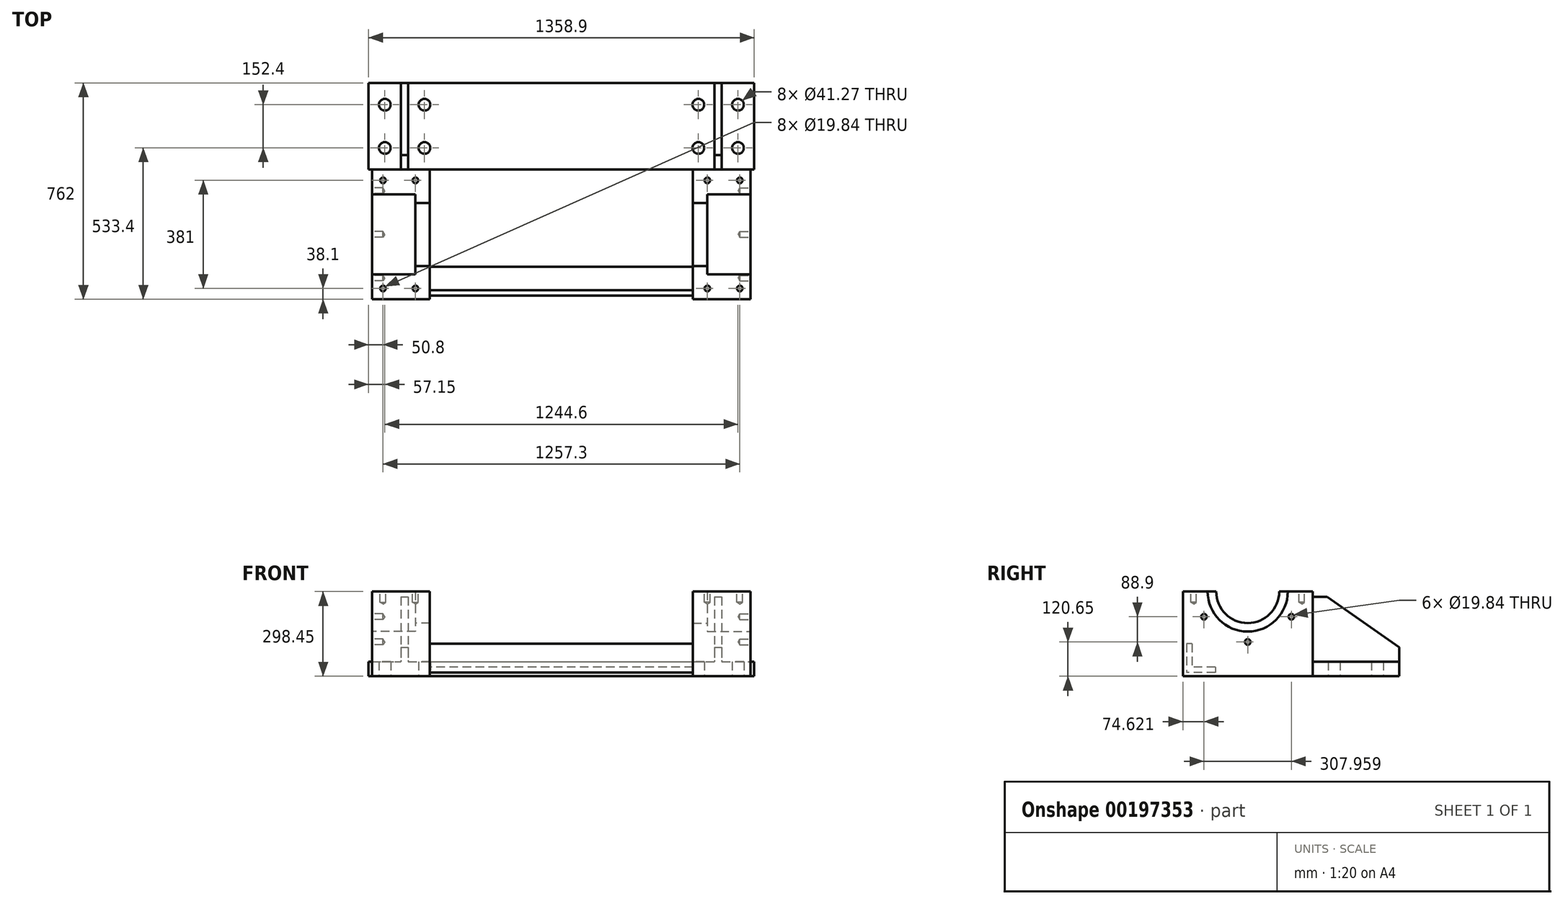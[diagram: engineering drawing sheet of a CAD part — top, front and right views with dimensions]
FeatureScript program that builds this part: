
annotation { "Feature Type Name" : "Feature", "Feature Type Description" : "" }
export const myFeature = defineFeature(function(context is Context, id is Id, definition is map)
    precondition{}
    {
        {
            var Q0;
            Q0=qCreatedBy(makeId("Top.planeOp"),FACE);
            var sketch = newSketch(context, id + "F0", { "sketchPlane" : qUnion([Q0])});
            skLineSegment(sketch, "E0.bottom", {"start": v(-679.45, 152.4) * mm, "end": v(679.45, 152.4) * mm});
            skLineSegment(sketch, "E0.top", {"start": v(-679.45, -152.4) * mm, "end": v(679.45, -152.4) * mm});
            skLineSegment(sketch, "E0.left", {"start": v(-679.45, 152.4) * mm, "end": v(-679.45, -152.4) * mm});
            skLineSegment(sketch, "E0.right", {"start": v(679.45, 152.4) * mm, "end": v(679.45, -152.4) * mm});
            skPoint(sketch, "E0.middle", {"position": v(0, 0) * mm});
            skLineSegment(sketch, "E1", {"start": v(0, 355.28) * mm, "end": v(0, -340.56) * mm, "construction": true});
            skLineSegment(sketch, "E2.0", {"start": v(-482.6, 355.28) * mm, "end": v(-482.6, -340.56) * mm, "construction": true});
            skLineSegment(sketch, "E3.0", {"start": v(-622.3, 355.28) * mm, "end": v(-622.3, -340.56) * mm, "construction": true});
            skLineSegment(sketch, "E4.0", {"start": v(-679.45, -76.2) * mm, "end": v(679.45, -76.2) * mm, "construction": true});
            skLineSegment(sketch, "E5.0", {"start": v(-679.45, 76.2) * mm, "end": v(679.45, 76.2) * mm, "construction": true});
            skCircle(sketch, "E6", {"center": v(-622.3, 76.2) * mm, "radius": 20.64 * mm});
            skCircle(sketch, "E7.0.1.0", {"center": v(-622.3, -76.2) * mm, "radius": 20.64 * mm});
            skCircle(sketch, "E7.1.0.0", {"center": v(-482.6, 76.2) * mm, "radius": 20.64 * mm});
            skCircle(sketch, "E7.1.1.0", {"center": v(-482.6, -76.2) * mm, "radius": 20.64 * mm});
            skLineSegment(sketch, "E7.direction1", {"start": v(-622.3, 76.2) * mm, "end": v(-482.6, 76.2) * mm, "construction": true});
            skLineSegment(sketch, "E7.direction2", {"start": v(-622.3, 76.2) * mm, "end": v(-622.3, -76.2) * mm, "construction": true});
            skLineSegment(sketch, "E8.MirrorCS", {"start": v(622.3, 76.2) * mm, "end": v(622.3, -76.2) * mm, "construction": true});
            skLineSegment(sketch, "E9.MirrorCS", {"start": v(622.3, 76.2) * mm, "end": v(482.6, 76.2) * mm, "construction": true});
            skCircle(sketch, "E10.MirrorC", {"center": v(482.6, -76.2) * mm, "radius": 20.64 * mm});
            skCircle(sketch, "E11.MirrorC", {"center": v(482.6, 76.2) * mm, "radius": 20.64 * mm});
            skCircle(sketch, "E12.MirrorC", {"center": v(622.3, -76.2) * mm, "radius": 20.64 * mm});
            skCircle(sketch, "E13.MirrorC", {"center": v(622.3, 76.2) * mm, "radius": 20.64 * mm});
            skSolve(sketch);
        }
        {
            var Q0;
            Q0 = qSketchRegion(id + "F0", true);
            extrude(context, id + "F1", {"entities" : qUnion([Q0]), "depth" : 50.8 * mm});
        }
        {
            var Q0;
            Q0=makeQuery(id+"F1.opExtrude","CAP_FACE",FACE,{"disambiguationData":[OSD([sQuery(id+"F0.wireOp",EDGE,"E0.bottom"),sQuery(id+"F0.wireOp",EDGE,"E0.top"),sQuery(id+"F0.wireOp",EDGE,"E0.left"),sQuery(id+"F0.wireOp",EDGE,"E0.right"),sQuery(id+"F0.wireOp",EDGE,"E6"),sQuery(id+"F0.wireOp",EDGE,"E7.0.1.0"),sQuery(id+"F0.wireOp",EDGE,"E7.1.0.0"),sQuery(id+"F0.wireOp",EDGE,"E7.1.1.0"),sQuery(id+"F0.wireOp",EDGE,"E10.MirrorC"),sQuery(id+"F0.wireOp",EDGE,"E11.MirrorC"),sQuery(id+"F0.wireOp",EDGE,"E12.MirrorC"),sQuery(id+"F0.wireOp",EDGE,"E13.MirrorC")])],"isStart":false});
            var sketch = newSketch(context, id + "F2", { "sketchPlane" : qUnion([Q0])});
            skLineSegment(sketch, "E14", {"start": v(0, 288.05) * mm, "end": v(0, -308.88) * mm, "construction": true});
            skLineSegment(sketch, "E15.0", {"start": v(-539.75, 288.05) * mm, "end": v(-539.75, -308.88) * mm, "construction": true});
            skLineSegment(sketch, "E16.0", {"start": v(-679.45, 152.4) * mm, "end": v(679.45, 152.4) * mm, "construction": true});
            skLineSegment(sketch, "E17.0", {"start": v(-679.45, -152.4) * mm, "end": v(679.45, -152.4) * mm, "construction": true});
            skLineSegment(sketch, "E18.bottom", {"start": v(-539.75, 152.4) * mm, "end": v(-565.15, 152.4) * mm});
            skLineSegment(sketch, "E18.top", {"start": v(-539.75, -152.4) * mm, "end": v(-565.15, -152.4) * mm});
            skLineSegment(sketch, "E18.left", {"start": v(-539.75, 152.4) * mm, "end": v(-539.75, -152.4) * mm});
            skLineSegment(sketch, "E18.right", {"start": v(-565.15, 152.4) * mm, "end": v(-565.15, -152.4) * mm});
            skLineSegment(sketch, "E19.MirrorCS", {"start": v(539.75, -152.4) * mm, "end": v(565.15, -152.4) * mm});
            skLineSegment(sketch, "E20.MirrorCS", {"start": v(539.75, 152.4) * mm, "end": v(565.15, 152.4) * mm});
            skLineSegment(sketch, "E21.MirrorCS", {"start": v(565.15, 152.4) * mm, "end": v(565.15, -152.4) * mm});
            skLineSegment(sketch, "E22.MirrorCS", {"start": v(539.75, 152.4) * mm, "end": v(539.75, -152.4) * mm});
            skSolve(sketch);
        }
        {
            var Q0;
            Q0 = qSketchRegion(id + "F2", true);
            extrude(context, id + "F3", {"entities" : qUnion([Q0]), "operationType" : NewBodyOperationType.ADD, "depth" : 228.6 * mm});
        }
        {
            var Q0;
            Q0=makeQuery(id+"F3.opExtrude","SWEPT_FACE",FACE,{"disambiguationData":[OSD([sQuery(id+"F2.wireOp",EDGE,"E21.MirrorCS")])]});
            var sketch = newSketch(context, id + "F4", { "sketchPlane" : qUnion([Q0])});
            skLineSegment(sketch, "E23.0", {"start": v(152.4, 50.8) * mm, "end": v(-152.4, 50.8) * mm, "construction": true});
            skLineSegment(sketch, "E24.0", {"start": v(-152.4, 279.4) * mm, "end": v(-152.4, 50.8) * mm, "construction": true});
            skLineSegment(sketch, "E25.0", {"start": v(-101.6, 279.4) * mm, "end": v(-101.6, 50.8) * mm, "construction": true});
            skLineSegment(sketch, "E26.0", {"start": v(152.4, 101.6) * mm, "end": v(-152.4, 101.6) * mm, "construction": true});
            skLineSegment(sketch, "E27", {"start": v(-101.6, 279.4) * mm, "end": v(152.4, 101.6) * mm});
            skLineSegment(sketch, "E28", {"start": v(152.4, 279.4) * mm, "end": v(152.4, 101.6) * mm});
            skLineSegment(sketch, "E29", {"start": v(152.4, 279.4) * mm, "end": v(-101.6, 279.4) * mm});
            skSolve(sketch);
        }
        {
            var Q0;
            Q0 = qSketchRegion(id + "F4", true);
            extrude(context, id + "F5", {"entities" : qUnion([Q0]), "operationType" : NewBodyOperationType.REMOVE, "endBound" : BoundingType.THROUGH_ALL, "oppositeDirection" : true, "depth" : 25.4 * mm});
        }
        {
            var Q0;
            Q0=makeQuery(id+"F1.opExtrude","CAP_FACE",FACE,{"disambiguationData":[OSD([sQuery(id+"F0.wireOp",EDGE,"E0.bottom"),sQuery(id+"F0.wireOp",EDGE,"E0.top"),sQuery(id+"F0.wireOp",EDGE,"E0.left"),sQuery(id+"F0.wireOp",EDGE,"E0.right"),sQuery(id+"F0.wireOp",EDGE,"E6"),sQuery(id+"F0.wireOp",EDGE,"E7.0.1.0"),sQuery(id+"F0.wireOp",EDGE,"E7.1.0.0"),sQuery(id+"F0.wireOp",EDGE,"E7.1.1.0"),sQuery(id+"F0.wireOp",EDGE,"E10.MirrorC"),sQuery(id+"F0.wireOp",EDGE,"E11.MirrorC"),sQuery(id+"F0.wireOp",EDGE,"E12.MirrorC"),sQuery(id+"F0.wireOp",EDGE,"E13.MirrorC")])],"isStart":true});
            var sketch = newSketch(context, id + "F6", { "sketchPlane" : qUnion([Q0])});
            skLineSegment(sketch, "E30", {"start": v(0, -264.01) * mm, "end": v(0, 609.6) * mm, "construction": true});
            skLineSegment(sketch, "E31.0", {"start": v(-679.45, 152.4) * mm, "end": v(679.45, 152.4) * mm, "construction": true});
            skLineSegment(sketch, "E32.0", {"start": v(-679.45, 609.6) * mm, "end": v(679.45, 609.6) * mm, "construction": true});
            skLineSegment(sketch, "E33.0", {"start": v(666.75, 152.4) * mm, "end": v(666.75, 609.6) * mm});
            skLineSegment(sketch, "E34.0", {"start": v(463.55, 152.4) * mm, "end": v(463.55, 609.6) * mm});
            skLineSegment(sketch, "E35.bottom", {"start": v(463.55, 152.4) * mm, "end": v(666.75, 152.4) * mm});
            skLineSegment(sketch, "E35.top", {"start": v(463.55, 609.6) * mm, "end": v(666.75, 609.6) * mm});
            skSolve(sketch);
        }
        {
            var Q0;
            Q0 = qSketchRegion(id + "F6", true);
            extrude(context, id + "F7", {"entities" : qUnion([Q0]), "oppositeDirection" : true, "depth" : 298.45 * mm});
        }
        {
            var Q0;
            Q0=makeQuery(id+"F7.opExtrude","SWEPT_FACE",FACE,{"disambiguationData":[OSD([sQuery(id+"F6.wireOp",EDGE,"E33.0")])]});
            var sketch = newSketch(context, id + "F8", { "sketchPlane" : qUnion([Q0])});
            skCircle(sketch, "E36", {"center": v(-381, 298.45) * mm, "radius": 141.29 * mm});
            skSolve(sketch);
        }
        {
            var Q0;
            Q0 = qSketchRegion(id + "F8", true);
            extrude(context, id + "F9", {"entities" : qUnion([Q0]), "operationType" : NewBodyOperationType.REMOVE, "oppositeDirection" : true, "depth" : 152.4 * mm});
        }
        {
            var Q0;
            Q0=makeQuery(id+"F9.boolean.opBoolean","COPY",FACE,{"derivedFrom":makeQuery(id+"F9.opExtrude","CAP_FACE",FACE,{"disambiguationData":[OSD([sQuery(id+"F8.wireOp",EDGE,"E36")])],"isStart":false})});
            var sketch = newSketch(context, id + "F10", { "sketchPlane" : qUnion([Q0])});
            skCircle(sketch, "E37", {"center": v(-381, 298.45) * mm, "radius": 111.13 * mm});
            skSolve(sketch);
        }
        {
            var Q0;
            Q0 = qSketchRegion(id + "F10", true);
            extrude(context, id + "F11", {"entities" : qUnion([Q0]), "operationType" : NewBodyOperationType.REMOVE, "endBound" : BoundingType.THROUGH_ALL, "oppositeDirection" : true, "depth" : 25.4 * mm});
        }
        {
            var Q0;
            Q0=makeQuery(id+"F7.opExtrude","SWEPT_FACE",FACE,{"disambiguationData":[OSD([sQuery(id+"F6.wireOp",EDGE,"E33.0")])]});
            var sketch = newSketch(context, id + "F12", { "sketchPlane" : qUnion([Q0])});
            skLineSegment(sketch, "E38", {"start": v(-522.29, 298.45) * mm, "end": v(-239.71, 298.45) * mm, "construction": true});
            skCircle(sketch, "E39", {"center": v(-381, 298.45) * mm, "radius": 177.8 * mm, "construction": true});
            skLineSegment(sketch, "E40", {"start": v(-381, 298.45) * mm, "end": v(-381, 120.65) * mm, "construction": true});
            skPoint(sketch, "E41", {"position": v(-381, 120.65) * mm});
            skPoint(sketch, "E42.1.0", {"position": v(-227.02, 209.55) * mm});
            skPoint(sketch, "E42.2.0", {"position": v(-227.02, 387.35) * mm});
            skPoint(sketch, "E42.3.0", {"position": v(-381, 476.25) * mm});
            skPoint(sketch, "E42.4.0", {"position": v(-534.98, 387.35) * mm});
            skPoint(sketch, "E42.5.0", {"position": v(-534.98, 209.55) * mm});
            skSolve(sketch);
        }
        {
            var Q0;
            Q0=sQuery(id+"F12.wireOp",VERTEX,"E42.5.0");
            var Q1;
            Q1=sQuery(id+"F12.wireOp",VERTEX,"E41");
            var Q2;
            Q2=sQuery(id+"F12.wireOp",VERTEX,"E42.1.0");
            var Q3;
            Q3=makeQuery(id+"F7.opExtrude","SWEPT_BODY",BODY,{"disambiguationData":[OSD([sQuery(id+"F6.wireOp",EDGE,"E35.bottom"),sQuery(id+"F6.wireOp",EDGE,"E35.top"),sQuery(id+"F6.wireOp",EDGE,"E34.0"),sQuery(id+"F6.wireOp",EDGE,"E33.0")])]});
            hole(context, id + "F13", {"style" : HoleStyle.SIMPLE, "endStyle" : HoleEndStyle.BLIND, "standardTappedOrClearance" : lookupTablePath({ "standard" : "ANSI", "fit" : "Normal (ASME)", "size" : "3/4", "type" : "Clearance" }), "standardBlindInLast" : lookupTablePath({ "fit" : "Free", "standard" : "ANSI", "size" : "3/4", "type" : "Clearance" }), "holeDiameter" : 19.84 * mm, "holeDepth" : 38.1 * mm, "locations" : qUnion([Q0, Q1, Q2]), "scope" : qUnion([Q3])});
        }
        {
            var Q0;
            {var subQ1=sQuery(id+"F6.wireOp",EDGE,"E33.0");var subQ2=sQuery(id+"F6.wireOp",EDGE,"E34.0");var subQ3=sQuery(id+"F6.wireOp",EDGE,"E35.top");Q0=makeQuery(id+"F11.boolean.opBoolean","SPLIT",FACE,{"disambiguationData":[TD([makeQuery(id+"F7.opExtrude","SWEPT_FACE",FACE,{"disambiguationData":[OSD([subQ3])]})])],"derivedFrom":makeQuery(id+"F7.opExtrude","CAP_FACE",FACE,{"disambiguationData":[OSD([sQuery(id+"F6.wireOp",EDGE,"E35.bottom"),subQ3,subQ2,subQ1])],"isStart":false})});}
            var sketch = newSketch(context, id + "F14", { "sketchPlane" : qUnion([Q0])});
            skLineSegment(sketch, "E43.0", {"start": v(666.75, -152.4) * mm, "end": v(666.75, -609.6) * mm, "construction": true});
            skLineSegment(sketch, "E44.0.0", {"start": v(514.35, -522.29) * mm, "end": v(514.35, -239.71) * mm, "construction": true});
            skLineSegment(sketch, "E44.0.1", {"start": v(666.75, -522.29) * mm, "end": v(514.35, -522.29) * mm, "construction": true});
            skLineSegment(sketch, "E44.0.2", {"start": v(666.75, -239.71) * mm, "end": v(666.75, -522.29) * mm, "construction": true});
            skLineSegment(sketch, "E44.0.3", {"start": v(666.75, -239.71) * mm, "end": v(514.35, -239.71) * mm, "construction": true});
            skLineSegment(sketch, "E45", {"start": v(514.35, -381) * mm, "end": v(666.75, -381) * mm, "construction": true});
            skLineSegment(sketch, "E46.0", {"start": v(463.55, -152.4) * mm, "end": v(666.75, -152.4) * mm, "construction": true});
            skLineSegment(sketch, "E47.0", {"start": v(463.55, -609.6) * mm, "end": v(666.75, -609.6) * mm, "construction": true});
            skLineSegment(sketch, "E48.0", {"start": v(628.65, -152.4) * mm, "end": v(628.65, -609.6) * mm, "construction": true});
            skLineSegment(sketch, "E49.0", {"start": v(514.35, -152.4) * mm, "end": v(514.35, -609.6) * mm, "construction": true});
            skLineSegment(sketch, "E50.0", {"start": v(514.35, -571.5) * mm, "end": v(628.65, -571.5) * mm, "construction": true});
            skPoint(sketch, "E51", {"position": v(514.35, -571.5) * mm});
            skPoint(sketch, "E52", {"position": v(628.65, -571.5) * mm});
            skPoint(sketch, "E53.MirrorP", {"position": v(514.35, -190.5) * mm});
            skPoint(sketch, "E54.MirrorP", {"position": v(628.65, -190.5) * mm});
            skSolve(sketch);
        }
        {
            var Q0;
            Q0=sQuery(id+"F14.wireOp",VERTEX,"E51");
            var Q1;
            Q1=sQuery(id+"F14.wireOp",VERTEX,"E52");
            var Q2;
            Q2=sQuery(id+"F14.wireOp",VERTEX,"E53.MirrorP");
            var Q3;
            Q3=sQuery(id+"F14.wireOp",VERTEX,"E54.MirrorP");
            var Q4;
            Q4=makeQuery(id+"F7.opExtrude","SWEPT_BODY",BODY,{"disambiguationData":[OSD([sQuery(id+"F6.wireOp",EDGE,"E35.bottom"),sQuery(id+"F6.wireOp",EDGE,"E35.top"),sQuery(id+"F6.wireOp",EDGE,"E34.0"),sQuery(id+"F6.wireOp",EDGE,"E33.0")])]});
            hole(context, id + "F15", {"style" : HoleStyle.SIMPLE, "endStyle" : HoleEndStyle.BLIND, "standardTappedOrClearance" : lookupTablePath({ "standard" : "ANSI", "fit" : "Normal (ASME)", "size" : "3/4", "type" : "Clearance" }), "standardBlindInLast" : lookupTablePath({ "fit" : "Free", "standard" : "ANSI", "size" : "3/4", "type" : "Clearance" }), "holeDiameter" : 19.84 * mm, "holeDepth" : 38.1 * mm, "locations" : qUnion([Q0, Q1, Q2, Q3]), "scope" : qUnion([Q4])});
        }
        {
            var Q0;
            Q0=makeQuery(id+"F7.opExtrude","SWEPT_BODY",BODY,{"disambiguationData":[OSD([sQuery(id+"F6.wireOp",EDGE,"E35.bottom"),sQuery(id+"F6.wireOp",EDGE,"E35.top"),sQuery(id+"F6.wireOp",EDGE,"E34.0"),sQuery(id+"F6.wireOp",EDGE,"E33.0")])]});
            var Q1;
            Q1=qCreatedBy(makeId("Right.planeOp"),FACE);
            mirror(context, id + "F16", {"operationType" : NewBodyOperationType.ADD, "entities" : qUnion([Q0]), "mirrorPlane" : qUnion([Q1])});
        }
        {
            var Q0;
            Q0=makeQuery(id+"F16.opPattern","COPY",FACE,{"derivedFrom":makeQuery(id+"F7.opExtrude","SWEPT_FACE",FACE,{"disambiguationData":[OSD([sQuery(id+"F6.wireOp",EDGE,"E34.0")])]}),"instanceName":"1"});
            var sketch = newSketch(context, id + "F17", { "sketchPlane" : qUnion([Q0])});
            skLineSegment(sketch, "E55.0", {"start": v(-495.3, 12.7) * mm, "end": v(-596.9, 12.7) * mm});
            skLineSegment(sketch, "E56.0", {"start": v(-596.9, 114.3) * mm, "end": v(-596.9, 12.7) * mm});
            skLineSegment(sketch, "E57.0", {"start": v(-577.85, 114.3) * mm, "end": v(-577.85, 31.75) * mm});
            skLineSegment(sketch, "E58.0", {"start": v(-495.3, 31.75) * mm, "end": v(-577.85, 31.75) * mm});
            skLineSegment(sketch, "E59.trimOffspring", {"start": v(-495.3, 31.75) * mm, "end": v(-495.3, 12.7) * mm});
            skLineSegment(sketch, "E60.trimOffspring", {"start": v(-577.85, 114.3) * mm, "end": v(-596.9, 114.3) * mm});
            skSolve(sketch);
        }
        {
            var Q0;
            Q0 = qSketchRegion(id + "F17", true);
            var Q1;
            Q1=makeQuery(id+"F7.opExtrude","SWEPT_FACE",FACE,{"disambiguationData":[OSD([sQuery(id+"F6.wireOp",EDGE,"E34.0")])]});
            extrude(context, id + "F18", {"entities" : qUnion([Q0]), "operationType" : NewBodyOperationType.ADD, "endBound" : BoundingType.UP_TO_SURFACE, "endBoundEntityFace" : qUnion([Q1]), "depth" : 25.4 * mm});
        }
    });
